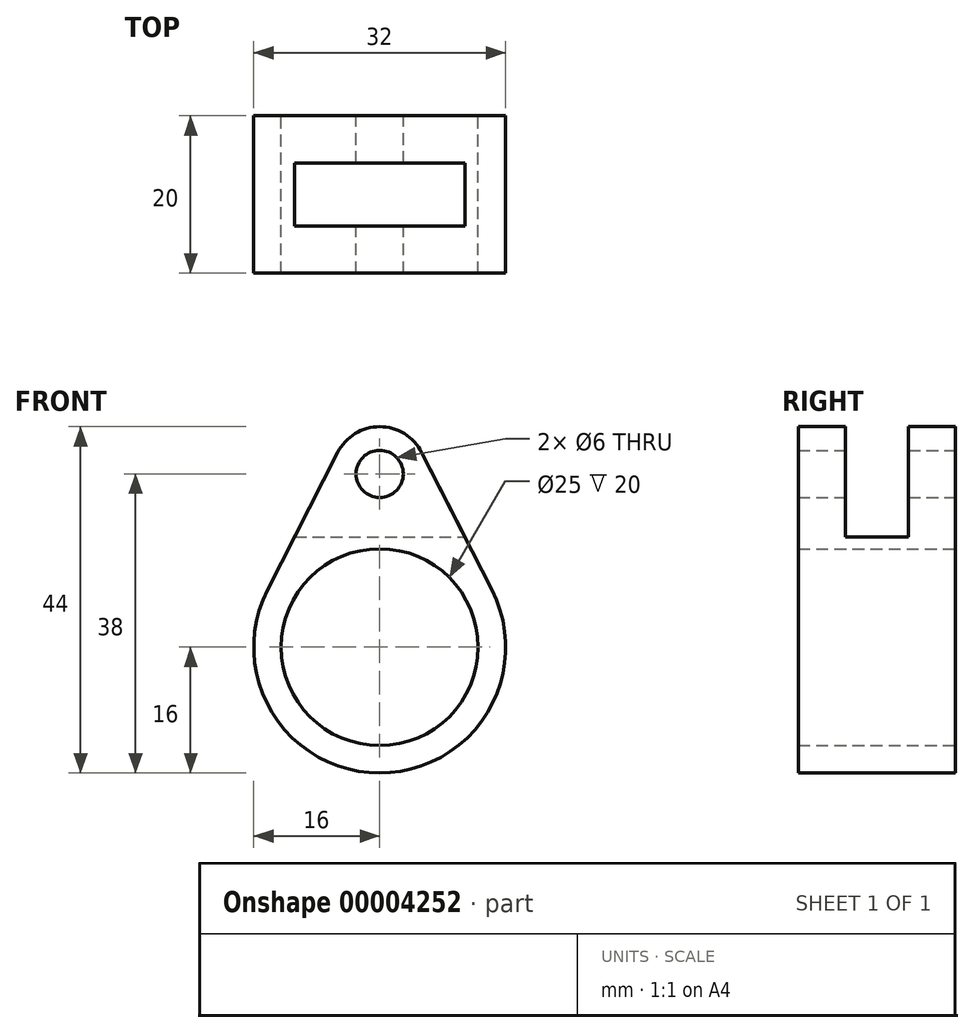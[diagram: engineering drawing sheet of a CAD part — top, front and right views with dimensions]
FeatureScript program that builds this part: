
annotation { "Feature Type Name" : "Feature", "Feature Type Description" : "" }
export const myFeature = defineFeature(function(context is Context, id is Id, definition is map)
    precondition{}
    {
        {
            var Q0;
            Q0=qCreatedBy(makeId("Front.planeOp"),FACE);
            var sketch = newSketch(context, id + "F0", { "sketchPlane" : qUnion([Q0])});
            skCircle(sketch, "E0", {"center": v(0, 0) * mm, "radius": 12.5 * mm});
            skArc(sketch, "E1", {"start": v(-14.25, 7.27) * mm, "mid": v(0, -16) * mm, "end": v(14.25, 7.27) * mm});
            skArc(sketch, "E2", {"start": v(5.34, 24.73) * mm, "mid": v(0, 28) * mm, "end": v(-5.34, 24.73) * mm});
            skLineSegment(sketch, "E3", {"start": v(-5.34, 24.73) * mm, "end": v(-14.25, 7.27) * mm});
            skLineSegment(sketch, "E4", {"start": v(5.34, 24.73) * mm, "end": v(14.25, 7.27) * mm});
            skCircle(sketch, "E5", {"center": v(0, 22) * mm, "radius": 3 * mm});
            skSolve(sketch);
        }
        {
            var Q0;
            Q0=makeQuery(id+"F0.imprint","IMPRINT",FACE,{"disambiguationData":[TD([[makeQuery(id+"F0.imprint","IMPRINT",EDGE,{"derivedFrom":sQuery(id+"F0.wireOp",EDGE,"E0")}),-1.0]])]});
            extrude(context, id + "F1", {"entities" : qUnion([Q0]), "depth" : 20 * mm, "symmetric" : true});
        }
        {
            var Q0;
            Q0=qCreatedBy(makeId("Front.planeOp"),FACE);
            var sketch = newSketch(context, id + "F2", { "sketchPlane" : qUnion([Q0])});
            skLineSegment(sketch, "E6.0", {"start": v(-5.34, 24.73) * mm, "end": v(-10.82, 14) * mm});
            skArc(sketch, "E7.0", {"start": v(5.34, 24.73) * mm, "mid": v(0, 28) * mm, "end": v(-5.34, 24.73) * mm});
            skLineSegment(sketch, "E8.0", {"start": v(5.34, 24.73) * mm, "end": v(10.82, 14) * mm});
            skLineSegment(sketch, "E9", {"start": v(-10.82, 14) * mm, "end": v(10.82, 14) * mm});
            skSolve(sketch);
        }
        {
            var Q0;
            Q0 = qSketchRegion(id + "F2", true);
            extrude(context, id + "F3", {"entities" : qUnion([Q0]), "operationType" : NewBodyOperationType.REMOVE, "oppositeDirection" : true, "depth" : 8 * mm, "symmetric" : true});
        }
    });
